# Revit family: Casement_34_B_Side_Hung_Standard
name_source: partatom
category: Windows
revit_build: Autodesk Revit 2014 (Build: 20130308_1515(x64)
units: mm (PartAtom-declared; Revit-internal decimal feet)

## types (18) — shared parameters
Aluminium Thickness = 1 mm  [stored 0.00328084 ft]
Bead SG Gap = 13 mm  [stored 0.0426509 ft]
Casement Dimension = 34 mm
Custom Sash Width = 554 mm  [stored 1.81759 ft]
DG Extrusion Start = 7 mm  [stored 0.0229659 ft]
DG Gasket Finish = Double Glazing Gasket Material
DG Thickness Calc = 4 mm  [stored 0.0131234 ft]
Default Sill Height = 800 mm  [stored 2.62467 ft]
Depth Bead = 20 mm  [stored 0.0656168 ft]
Description = Casement 34
Frame Center Offset = 17 mm
Limit Fixed Panel Width Max = 1500 mm
Limit Fixed Panel Width Min = 200 mm  [stored 0.656168 ft]
Limit Sash Height Max = 1500 mm
Limit Sash Height Min = 300 mm  [stored 0.984252 ft]
Limit Sash Width Max = 700 mm  [stored 2.29659 ft]
Limit Sash Width Min = 300 mm  [stored 0.984252 ft]
Limit Window Height Max = 1546 mm
Limit Window Height Min = 346 mm
Limit Window Width Max = 2129 mm
Limit Window Width Min = 829 mm  [stored 2.71982 ft]
Manufacturer = Crealco
Max System DG One Piece Thickness = 4 mm  [stored 0.0131234 ft]
Max System DG Unit Thickness = 20 mm  [stored 0.0656168 ft]
Model = Window 34mm, Type B side hung
Offset Bead SG Center Reversed = 17 mm
Offset Mullion Left = 569 mm  [stored 1.8668 ft]
Offset Panel 4 Left = 599 mm  [stored 1.96522 ft]
Offset Sash Left = 23 mm  [stored 0.0754593 ft]
Offset Sash Top = 23 mm  [stored 0.0754593 ft]
Offset Window Exterior = 17 mm
SG Gasket Thickness = 6 mm  [stored 0.019685 ft]
Sash Center Offset = 14 mm  [stored 0.0459318 ft]
Sash Overlap = 7 mm  [stored 0.0229659 ft]
Sash Spacing Inner = 8 mm  [stored 0.0262467 ft]
URL = http://www.crealco.co.za
Wall Closure = By host
Width Bead = 15 mm  [stored 0.0492126 ft]
Width Panel 1 = 539 mm  [stored 1.76837 ft]
Width Profile = 30 mm  [stored 0.0984252 ft]
Width Sash = 524 mm  [stored 1.71916 ft]
Width Sash Opening = 554 mm  [stored 1.81759 ft]
zero-valued in all types: Window Exterior Offset

## per-type parameters (varying)
- 34-0909S-1000Pa: Area Pane Left=0.37 m²; Area Pane Right=0.21 m²; Clearvue Insulated LowE SHGC Value=0.465; Clearvue Insulated LowE U Value=3.68; Clearvue Insulated SHGC Value=0.511; Clearvue Insulated U Value=4.26; Clearvue SHGC Value=0.574; Clearvue U Value=6.15; Custom Windload=1000 mm  [stored 3.28084 ft]; Custom Window Height=890 mm  [stored 2.91995 ft]; Custom Window Width=890 mm  [stored 2.91995 ft]; Depth Mullion=35 mm; Energy Advantage SHGC Value=0.514; Energy Advantage U Value=4.79; Height=890 mm  [stored 2.91995 ft]; Height Panel 4=830 mm  [stored 2.7231 ft]; Height Sash=814 mm  [stored 2.6706 ft]; Height Sash Opening=844 mm  [stored 2.76903 ft]; Intruderprufe LowE SHGC Value=0.482; Intruderprufe LowE U Value=4.63; Intruderprufe SHGC Value=0.542; Intruderprufe U Value=6.1; Length Mullion=890 mm  [stored 2.91995 ft]; Max Pane Area=0.37 m²; Mullion Depth Windload Based=35 mm; Width=890 mm  [stored 2.91995 ft]; Width Panel 4=261 mm  [stored 0.856299 ft]; Windload Design=1000 mm  [stored 3.28084 ft]
- 34-0909S-1500Pa: Area Pane Left=0.37 m²; Area Pane Right=0.21 m²; Clearvue Insulated LowE SHGC Value=0.465; Clearvue Insulated LowE U Value=3.68; Clearvue Insulated SHGC Value=0.511; Clearvue Insulated U Value=4.26; Clearvue SHGC Value=0.574; Clearvue U Value=6.15; Custom Windload=1500 mm; Custom Window Height=890 mm  [stored 2.91995 ft]; Custom Window Width=890 mm  [stored 2.91995 ft]; Depth Mullion=35 mm; Energy Advantage SHGC Value=0.514; Energy Advantage U Value=4.79; Height=890 mm  [stored 2.91995 ft]; Height Panel 4=830 mm  [stored 2.7231 ft]; Height Sash=814 mm  [stored 2.6706 ft]; Height Sash Opening=844 mm  [stored 2.76903 ft]; Intruderprufe LowE SHGC Value=0.482; Intruderprufe LowE U Value=4.63; Intruderprufe SHGC Value=0.542; Intruderprufe U Value=6.1; Length Mullion=890 mm  [stored 2.91995 ft]; Max Pane Area=0.37 m²; Mullion Depth Windload Based=35 mm; Width=890 mm  [stored 2.91995 ft]; Width Panel 4=261 mm  [stored 0.856299 ft]; Windload Design=1500 mm
- 34-0909S-2000Pa: Area Pane Left=0.37 m²; Area Pane Right=0.21 m²; Clearvue Insulated LowE SHGC Value=0.465; Clearvue Insulated LowE U Value=3.68; Clearvue Insulated SHGC Value=0.511; Clearvue Insulated U Value=4.26; Clearvue SHGC Value=0.574; Clearvue U Value=6.15; Custom Windload=2000 mm; Custom Window Height=890 mm  [stored 2.91995 ft]; Custom Window Width=890 mm  [stored 2.91995 ft]; Depth Mullion=35 mm; Energy Advantage SHGC Value=0.514; Energy Advantage U Value=4.79; Height=890 mm  [stored 2.91995 ft]; Height Panel 4=830 mm  [stored 2.7231 ft]; Height Sash=814 mm  [stored 2.6706 ft]; Height Sash Opening=844 mm  [stored 2.76903 ft]; Intruderprufe LowE SHGC Value=0.482; Intruderprufe LowE U Value=4.63; Intruderprufe SHGC Value=0.542; Intruderprufe U Value=6.1; Length Mullion=890 mm  [stored 2.91995 ft]; Max Pane Area=0.37 m²; Mullion Depth Windload Based=35 mm; Width=890 mm  [stored 2.91995 ft]; Width Panel 4=261 mm  [stored 0.856299 ft]; Windload Design=2000 mm
- 34-1209S-1000Pa: Area Pane Left=0.37 m²; Area Pane Right=0.45 m²; Clearvue Insulated LowE SHGC Value=0.502; Clearvue Insulated LowE U Value=3.38; Clearvue Insulated SHGC Value=0.552; Clearvue Insulated U Value=3.99; Clearvue SHGC Value=0.621; Clearvue U Value=6.1; Custom Windload=1000 mm  [stored 3.28084 ft]; Custom Window Height=890 mm  [stored 2.91995 ft]; Custom Window Width=1190 mm  [stored 3.9042 ft]; Depth Mullion=35 mm; Energy Advantage SHGC Value=0.556; Energy Advantage U Value=4.6; Height=890 mm  [stored 2.91995 ft]; Height Panel 4=830 mm  [stored 2.7231 ft]; Height Sash=814 mm  [stored 2.6706 ft]; Height Sash Opening=844 mm  [stored 2.76903 ft]; Intruderprufe LowE SHGC Value=0.521; Intruderprufe LowE U Value=4.41; Intruderprufe SHGC Value=0.587; Intruderprufe U Value=6.02; Length Mullion=890 mm  [stored 2.91995 ft]; Max Pane Area=0.45 m²; Mullion Depth Windload Based=35 mm; Width=1190 mm  [stored 3.9042 ft]; Width Panel 4=561 mm; Windload Design=1000 mm  [stored 3.28084 ft]
- 34-1209S-1500Pa: Area Pane Left=0.37 m²; Area Pane Right=0.45 m²; Clearvue Insulated LowE SHGC Value=0.502; Clearvue Insulated LowE U Value=3.38; Clearvue Insulated SHGC Value=0.552; Clearvue Insulated U Value=3.99; Clearvue SHGC Value=0.621; Clearvue U Value=6.1; Custom Windload=1500 mm; Custom Window Height=890 mm  [stored 2.91995 ft]; Custom Window Width=1190 mm  [stored 3.9042 ft]; Depth Mullion=35 mm; Energy Advantage SHGC Value=0.556; Energy Advantage U Value=4.6; Height=890 mm  [stored 2.91995 ft]; Height Panel 4=830 mm  [stored 2.7231 ft]; Height Sash=814 mm  [stored 2.6706 ft]; Height Sash Opening=844 mm  [stored 2.76903 ft]; Intruderprufe LowE SHGC Value=0.521; Intruderprufe LowE U Value=4.41; Intruderprufe SHGC Value=0.587; Intruderprufe U Value=6.02; Length Mullion=890 mm  [stored 2.91995 ft]; Max Pane Area=0.45 m²; Mullion Depth Windload Based=35 mm; Width=1190 mm  [stored 3.9042 ft]; Width Panel 4=561 mm; Windload Design=1500 mm
- 34-1209S-2000Pa: Area Pane Left=0.37 m²; Area Pane Right=0.45 m²; Clearvue Insulated LowE SHGC Value=0.502; Clearvue Insulated LowE U Value=3.38; Clearvue Insulated SHGC Value=0.552; Clearvue Insulated U Value=3.99; Clearvue SHGC Value=0.621; Clearvue U Value=6.1; Custom Windload=2000 mm; Custom Window Height=890 mm  [stored 2.91995 ft]; Custom Window Width=1190 mm  [stored 3.9042 ft]; Depth Mullion=35 mm; Energy Advantage SHGC Value=0.556; Energy Advantage U Value=4.6; Height=890 mm  [stored 2.91995 ft]; Height Panel 4=830 mm  [stored 2.7231 ft]; Height Sash=814 mm  [stored 2.6706 ft]; Height Sash Opening=844 mm  [stored 2.76903 ft]; Intruderprufe LowE SHGC Value=0.521; Intruderprufe LowE U Value=4.41; Intruderprufe SHGC Value=0.587; Intruderprufe U Value=6.02; Length Mullion=890 mm  [stored 2.91995 ft]; Max Pane Area=0.45 m²; Mullion Depth Windload Based=35 mm; Width=1190 mm  [stored 3.9042 ft]; Width Panel 4=561 mm; Windload Design=2000 mm
- 34-1509S-1000Pa: Area Pane Left=0.37 m²; Area Pane Right=0.7 m²; Clearvue Insulated LowE SHGC Value=0.524; Clearvue Insulated LowE U Value=3.2; Clearvue Insulated SHGC Value=0.576; Clearvue Insulated U Value=3.82; Clearvue SHGC Value=0.65; Clearvue U Value=6.07; Custom Windload=1000 mm  [stored 3.28084 ft]; Custom Window Height=890 mm  [stored 2.91995 ft]; Custom Window Width=1490 mm  [stored 4.88845 ft]; Depth Mullion=35 mm; Energy Advantage SHGC Value=0.581; Energy Advantage U Value=4.49; Height=890 mm  [stored 2.91995 ft]; Height Panel 4=830 mm  [stored 2.7231 ft]; Height Sash=814 mm  [stored 2.6706 ft]; Height Sash Opening=844 mm  [stored 2.76903 ft]; Intruderprufe LowE SHGC Value=0.543; Intruderprufe LowE U Value=4.29; Intruderprufe SHGC Value=0.614; Intruderprufe U Value=5.98; Length Mullion=890 mm  [stored 2.91995 ft]; Max Pane Area=0.7 m²; Mullion Depth Windload Based=35 mm; Width=1490 mm  [stored 4.88845 ft]; Width Panel 4=861 mm  [stored 2.8248 ft]; Windload Design=1000 mm  [stored 3.28084 ft]
- 34-1509S-1500Pa: Area Pane Left=0.37 m²; Area Pane Right=0.7 m²; Clearvue Insulated LowE SHGC Value=0.524; Clearvue Insulated LowE U Value=3.2; Clearvue Insulated SHGC Value=0.576; Clearvue Insulated U Value=3.82; Clearvue SHGC Value=0.65; Clearvue U Value=6.07; Custom Windload=1500 mm; Custom Window Height=890 mm  [stored 2.91995 ft]; Custom Window Width=1490 mm  [stored 4.88845 ft]; Depth Mullion=35 mm; Energy Advantage SHGC Value=0.581; Energy Advantage U Value=4.49; Height=890 mm  [stored 2.91995 ft]; Height Panel 4=830 mm  [stored 2.7231 ft]; Height Sash=814 mm  [stored 2.6706 ft]; Height Sash Opening=844 mm  [stored 2.76903 ft]; Intruderprufe LowE SHGC Value=0.543; Intruderprufe LowE U Value=4.29; Intruderprufe SHGC Value=0.614; Intruderprufe U Value=5.98; Length Mullion=890 mm  [stored 2.91995 ft]; Max Pane Area=0.7 m²; Mullion Depth Windload Based=35 mm; Width=1490 mm  [stored 4.88845 ft]; Width Panel 4=861 mm  [stored 2.8248 ft]; Windload Design=1500 mm
- 34-1509S-2000Pa: Area Pane Left=0.37 m²; Area Pane Right=0.7 m²; Clearvue Insulated LowE SHGC Value=0.524; Clearvue Insulated LowE U Value=3.2; Clearvue Insulated SHGC Value=0.576; Clearvue Insulated U Value=3.82; Clearvue SHGC Value=0.65; Clearvue U Value=6.07; Custom Windload=2000 mm; Custom Window Height=890 mm  [stored 2.91995 ft]; Custom Window Width=1490 mm  [stored 4.88845 ft]; Depth Mullion=35 mm; Energy Advantage SHGC Value=0.581; Energy Advantage U Value=4.49; Height=890 mm  [stored 2.91995 ft]; Height Panel 4=830 mm  [stored 2.7231 ft]; Height Sash=814 mm  [stored 2.6706 ft]; Height Sash Opening=844 mm  [stored 2.76903 ft]; Intruderprufe LowE SHGC Value=0.543; Intruderprufe LowE U Value=4.29; Intruderprufe SHGC Value=0.614; Intruderprufe U Value=5.98; Length Mullion=890 mm  [stored 2.91995 ft]; Max Pane Area=0.7 m²; Mullion Depth Windload Based=35 mm; Width=1490 mm  [stored 4.88845 ft]; Width Panel 4=861 mm  [stored 2.8248 ft]; Windload Design=2000 mm
- 34-0912S-1000Pa: Area Pane Left=0.52 m²; Area Pane Right=0.28 m²; Clearvue Insulated LowE SHGC Value=0.483; Clearvue Insulated LowE U Value=3.56; Clearvue Insulated SHGC Value=0.53; Clearvue Insulated U Value=4.15; Clearvue SHGC Value=0.596; Clearvue U Value=6.13; Custom Windload=1000 mm  [stored 3.28084 ft]; Custom Window Height=1190 mm  [stored 3.9042 ft]; Custom Window Width=890 mm  [stored 2.91995 ft]; Depth Mullion=35 mm; Energy Advantage SHGC Value=0.534; Energy Advantage U Value=4.71; Height=1190 mm  [stored 3.9042 ft]; Height Panel 4=1130 mm  [stored 3.70735 ft]; Height Sash=1114 mm  [stored 3.65486 ft]; Height Sash Opening=1144 mm; Intruderprufe LowE SHGC Value=0.5; Intruderprufe LowE U Value=4.56; Intruderprufe SHGC Value=0.564; Intruderprufe U Value=6.08; Length Mullion=1190 mm  [stored 3.9042 ft]; Max Pane Area=0.52 m²; Mullion Depth Windload Based=35 mm; Width=890 mm  [stored 2.91995 ft]; Width Panel 4=261 mm  [stored 0.856299 ft]; Windload Design=1000 mm  [stored 3.28084 ft]
- 34-0912S-1500Pa: Area Pane Left=0.52 m²; Area Pane Right=0.28 m²; Clearvue Insulated LowE SHGC Value=0.483; Clearvue Insulated LowE U Value=3.56; Clearvue Insulated SHGC Value=0.53; Clearvue Insulated U Value=4.15; Clearvue SHGC Value=0.596; Clearvue U Value=6.13; Custom Windload=1500 mm; Custom Window Height=1190 mm  [stored 3.9042 ft]; Custom Window Width=890 mm  [stored 2.91995 ft]; Depth Mullion=35 mm; Energy Advantage SHGC Value=0.534; Energy Advantage U Value=4.71; Height=1190 mm  [stored 3.9042 ft]; Height Panel 4=1130 mm  [stored 3.70735 ft]; Height Sash=1114 mm  [stored 3.65486 ft]; Height Sash Opening=1144 mm; Intruderprufe LowE SHGC Value=0.5; Intruderprufe LowE U Value=4.56; Intruderprufe SHGC Value=0.564; Intruderprufe U Value=6.08; Length Mullion=1190 mm  [stored 3.9042 ft]; Max Pane Area=0.52 m²; Mullion Depth Windload Based=35 mm; Width=890 mm  [stored 2.91995 ft]; Width Panel 4=261 mm  [stored 0.856299 ft]; Windload Design=1500 mm
- 34-0912S-2000Pa: Area Pane Left=0.52 m²; Area Pane Right=0.28 m²; Clearvue Insulated LowE SHGC Value=0.483; Clearvue Insulated LowE U Value=3.56; Clearvue Insulated SHGC Value=0.53; Clearvue Insulated U Value=4.15; Clearvue SHGC Value=0.596; Clearvue U Value=6.13; Custom Windload=2000 mm; Custom Window Height=1190 mm  [stored 3.9042 ft]; Custom Window Width=890 mm  [stored 2.91995 ft]; Depth Mullion=54 mm  [stored 0.177165 ft]; Energy Advantage SHGC Value=0.534; Energy Advantage U Value=4.71; Height=1190 mm  [stored 3.9042 ft]; Height Panel 4=1130 mm  [stored 3.70735 ft]; Height Sash=1114 mm  [stored 3.65486 ft]; Height Sash Opening=1144 mm; Intruderprufe LowE SHGC Value=0.5; Intruderprufe LowE U Value=4.56; Intruderprufe SHGC Value=0.564; Intruderprufe U Value=6.08; Length Mullion=1190 mm  [stored 3.9042 ft]; Max Pane Area=0.52 m²; Mullion Depth Windload Based=54 mm  [stored 0.177165 ft]; Width=890 mm  [stored 2.91995 ft]; Width Panel 4=261 mm  [stored 0.856299 ft]; Windload Design=2000 mm
- 34-1212S-1000Pa: Area Pane Left=0.52 m²; Area Pane Right=0.62 m²; Clearvue Insulated LowE SHGC Value=0.519; Clearvue Insulated LowE U Value=3.25; Clearvue Insulated SHGC Value=0.571; Clearvue Insulated U Value=3.88; Clearvue SHGC Value=0.644; Clearvue U Value=6.08; Custom Windload=1000 mm  [stored 3.28084 ft]; Custom Window Height=1190 mm  [stored 3.9042 ft]; Custom Window Width=1190 mm  [stored 3.9042 ft]; Depth Mullion=35 mm; Energy Advantage SHGC Value=0.576; Energy Advantage U Value=4.52; Height=1190 mm  [stored 3.9042 ft]; Height Panel 4=1130 mm  [stored 3.70735 ft]; Height Sash=1114 mm  [stored 3.65486 ft]; Height Sash Opening=1144 mm; Intruderprufe LowE SHGC Value=0.539; Intruderprufe LowE U Value=4.35; Intruderprufe SHGC Value=0.609; Intruderprufe U Value=6.01; Length Mullion=1190 mm  [stored 3.9042 ft]; Max Pane Area=0.62 m²; Mullion Depth Windload Based=35 mm; Width=1190 mm  [stored 3.9042 ft]; Width Panel 4=561 mm; Windload Design=1000 mm  [stored 3.28084 ft]
- 34-1212S-1500Pa: Area Pane Left=0.52 m²; Area Pane Right=0.62 m²; Clearvue Insulated LowE SHGC Value=0.521; Clearvue Insulated LowE U Value=3.37; Clearvue Insulated SHGC Value=0.586; Clearvue Insulated U Value=3.8; Clearvue SHGC Value=0.644; Clearvue U Value=6.15; Custom Windload=1500 mm; Custom Window Height=1190 mm  [stored 3.9042 ft]; Custom Window Width=1190 mm  [stored 3.9042 ft]; Depth Mullion=54 mm  [stored 0.177165 ft]; Energy Advantage SHGC Value=0.577; Energy Advantage U Value=4.61; Height=1190 mm  [stored 3.9042 ft]; Height Panel 4=1130 mm  [stored 3.70735 ft]; Height Sash=1114 mm  [stored 3.65486 ft]; Height Sash Opening=1144 mm; Intruderprufe LowE SHGC Value=0.541; Intruderprufe LowE U Value=4.45; Intruderprufe SHGC Value=0.607; Intruderprufe U Value=5.84; Length Mullion=1190 mm  [stored 3.9042 ft]; Max Pane Area=0.62 m²; Mullion Depth Windload Based=54 mm  [stored 0.177165 ft]; Width=1190 mm  [stored 3.9042 ft]; Width Panel 4=561 mm; Windload Design=1500 mm
- 34-1212S-2000Pa: Area Pane Left=0.52 m²; Area Pane Right=0.62 m²; Clearvue Insulated LowE SHGC Value=0.521; Clearvue Insulated LowE U Value=3.37; Clearvue Insulated SHGC Value=0.586; Clearvue Insulated U Value=3.8; Clearvue SHGC Value=0.644; Clearvue U Value=6.15; Custom Windload=2000 mm; Custom Window Height=1190 mm  [stored 3.9042 ft]; Custom Window Width=1190 mm  [stored 3.9042 ft]; Depth Mullion=54 mm  [stored 0.177165 ft]; Energy Advantage SHGC Value=0.577; Energy Advantage U Value=4.61; Height=1190 mm  [stored 3.9042 ft]; Height Panel 4=1130 mm  [stored 3.70735 ft]; Height Sash=1114 mm  [stored 3.65486 ft]; Height Sash Opening=1144 mm; Intruderprufe LowE SHGC Value=0.541; Intruderprufe LowE U Value=4.45; Intruderprufe SHGC Value=0.607; Intruderprufe U Value=5.84; Length Mullion=1190 mm  [stored 3.9042 ft]; Max Pane Area=0.62 m²; Mullion Depth Windload Based=54 mm  [stored 0.177165 ft]; Width=1190 mm  [stored 3.9042 ft]; Width Panel 4=561 mm; Windload Design=2000 mm
- 34-1512S-1000Pa: Area Pane Left=0.52 m²; Area Pane Right=0.95 m²; Clearvue Insulated LowE SHGC Value=0.542; Clearvue Insulated LowE U Value=3.07; Clearvue Insulated SHGC Value=0.596; Clearvue Insulated U Value=3.72; Clearvue SHGC Value=0.672; Clearvue U Value=6.05; Custom Windload=1000 mm  [stored 3.28084 ft]; Custom Window Height=1190 mm  [stored 3.9042 ft]; Custom Window Width=1490 mm  [stored 4.88845 ft]; Depth Mullion=35 mm; Energy Advantage SHGC Value=0.601; Energy Advantage U Value=4.41; Height=1190 mm  [stored 3.9042 ft]; Height Panel 4=1130 mm  [stored 3.70735 ft]; Height Sash=1114 mm  [stored 3.65486 ft]; Height Sash Opening=1144 mm; Intruderprufe LowE SHGC Value=0.561; Intruderprufe LowE U Value=4.23; Intruderprufe SHGC Value=0.636; Intruderprufe U Value=5.96; Length Mullion=1190 mm  [stored 3.9042 ft]; Max Pane Area=0.95 m²; Mullion Depth Windload Based=35 mm; Width=1490 mm  [stored 4.88845 ft]; Width Panel 4=861 mm  [stored 2.8248 ft]; Windload Design=1000 mm  [stored 3.28084 ft]
- 34-1512S-1500Pa: Area Pane Left=0.52 m²; Area Pane Right=0.95 m²; Clearvue Insulated LowE SHGC Value=0.543; Clearvue Insulated LowE U Value=3.16; Clearvue Insulated SHGC Value=0.607; Clearvue Insulated U Value=3.65; Clearvue SHGC Value=0.672; Clearvue U Value=6.11; Custom Windload=1500 mm; Custom Window Height=1190 mm  [stored 3.9042 ft]; Custom Window Width=1490 mm  [stored 4.88845 ft]; Depth Mullion=54 mm  [stored 0.177165 ft]; Energy Advantage SHGC Value=0.602; Energy Advantage U Value=4.48; Height=1190 mm  [stored 3.9042 ft]; Height Panel 4=1130 mm  [stored 3.70735 ft]; Height Sash=1114 mm  [stored 3.65486 ft]; Height Sash Opening=1144 mm; Intruderprufe LowE SHGC Value=0.563; Intruderprufe LowE U Value=4.31; Intruderprufe SHGC Value=0.634; Intruderprufe U Value=5.83; Length Mullion=1190 mm  [stored 3.9042 ft]; Max Pane Area=0.95 m²; Mullion Depth Windload Based=54 mm  [stored 0.177165 ft]; Width=1490 mm  [stored 4.88845 ft]; Width Panel 4=861 mm  [stored 2.8248 ft]; Windload Design=1500 mm
- 34-1512S-2000Pa: Area Pane Left=0.52 m²; Area Pane Right=0.95 m²; Clearvue Insulated LowE SHGC Value=0.543; Clearvue Insulated LowE U Value=3.16; Clearvue Insulated SHGC Value=0.607; Clearvue Insulated U Value=3.65; Clearvue SHGC Value=0.672; Clearvue U Value=6.11; Custom Windload=2000 mm; Custom Window Height=1190 mm  [stored 3.9042 ft]; Custom Window Width=1490 mm  [stored 4.88845 ft]; Depth Mullion=54 mm  [stored 0.177165 ft]; Energy Advantage SHGC Value=0.602; Energy Advantage U Value=4.48; Height=1190 mm  [stored 3.9042 ft]; Height Panel 4=1130 mm  [stored 3.70735 ft]; Height Sash=1114 mm  [stored 3.65486 ft]; Height Sash Opening=1144 mm; Intruderprufe LowE SHGC Value=0.563; Intruderprufe LowE U Value=4.31; Intruderprufe SHGC Value=0.634; Intruderprufe U Value=5.83; Length Mullion=1190 mm  [stored 3.9042 ft]; Max Pane Area=0.95 m²; Mullion Depth Windload Based=54 mm  [stored 0.177165 ft]; Width=1490 mm  [stored 4.88845 ft]; Width Panel 4=861 mm  [stored 2.8248 ft]; Windload Design=2000 mm

note: [stored X ft] marks values corroborated as IEEE doubles in the binary element streams (Revit-internal decimal feet)

## geometry (parser evidence)
native form markers: Extrusion x1, Sweep x28
no freeform markers — native parametric forms only
